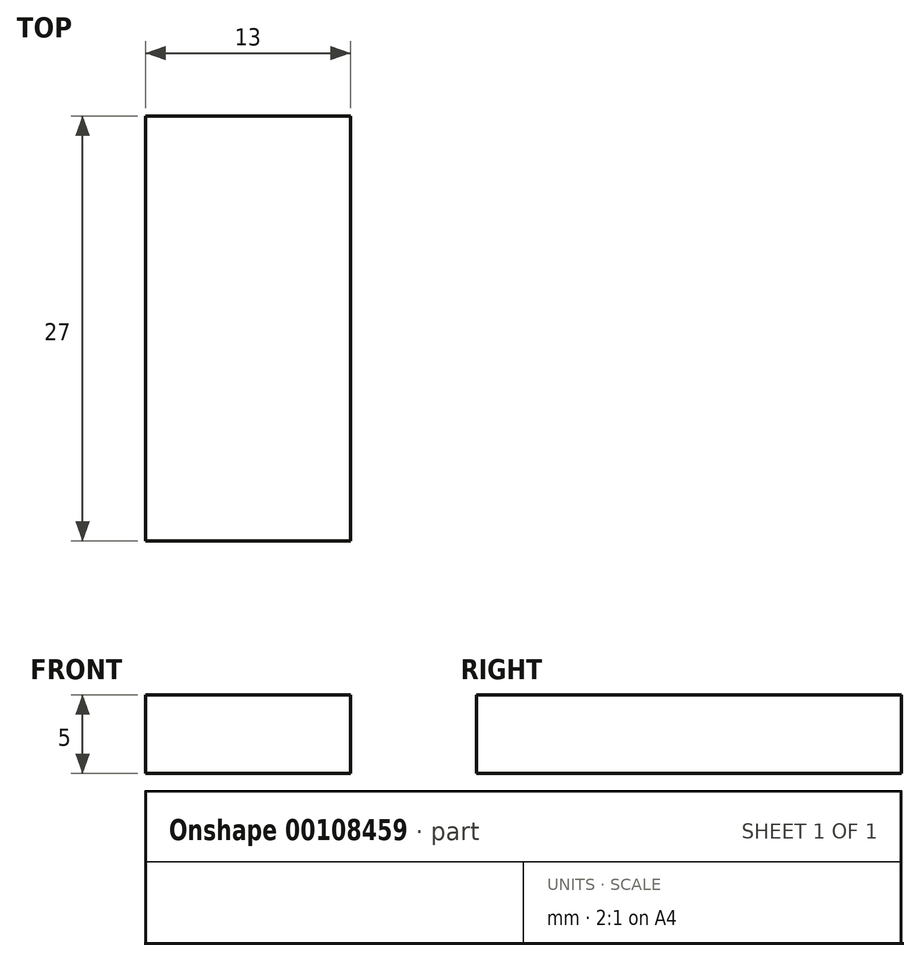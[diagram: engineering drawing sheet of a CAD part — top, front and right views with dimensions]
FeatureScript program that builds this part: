
annotation { "Feature Type Name" : "Feature", "Feature Type Description" : "" }
export const myFeature = defineFeature(function(context is Context, id is Id, definition is map)
    precondition{}
    {
        {
            var Q0;
            Q0=qCreatedBy(makeId("Top.planeOp"),FACE);
            var sketch = newSketch(context, id + "F0", { "sketchPlane" : qUnion([Q0])});
            skLineSegment(sketch, "E0.bottom", {"start": v(6.5, 13.5) * mm, "end": v(-6.5, 13.5) * mm});
            skLineSegment(sketch, "E0.top", {"start": v(6.5, -13.5) * mm, "end": v(-6.5, -13.5) * mm});
            skLineSegment(sketch, "E0.left", {"start": v(6.5, 13.5) * mm, "end": v(6.5, -13.5) * mm});
            skLineSegment(sketch, "E0.right", {"start": v(-6.5, 13.5) * mm, "end": v(-6.5, -13.5) * mm});
            skPoint(sketch, "E0.middle", {"position": v(0, 0) * mm});
            skSolve(sketch);
        }
        {
            var Q0;
            Q0 = qSketchRegion(id + "F0", true);
            extrude(context, id + "F1", {"entities" : qUnion([Q0]), "depth" : 5 * mm});
        }
    });
